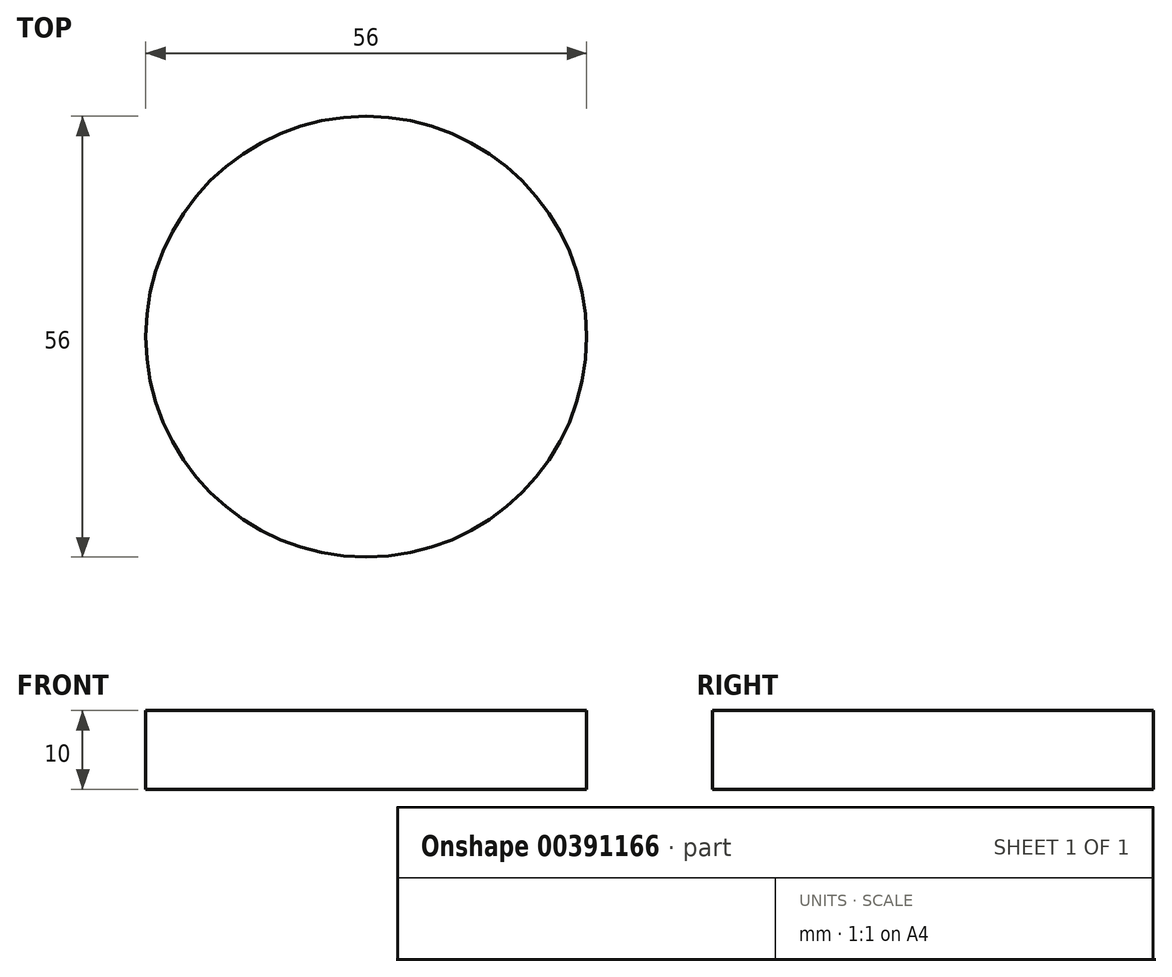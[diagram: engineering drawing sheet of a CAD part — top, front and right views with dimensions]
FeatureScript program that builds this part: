
annotation { "Feature Type Name" : "Feature", "Feature Type Description" : "" }
export const myFeature = defineFeature(function(context is Context, id is Id, definition is map)
    precondition{}
    {
        {
            var Q0;
            Q0=qCreatedBy(makeId("Top.planeOp"),FACE);
            var sketch = newSketch(context, id + "F0", { "sketchPlane" : qUnion([Q0])});
            skCircle(sketch, "E0", {"center": v(0, 0) * mm, "radius": 28 * mm});
            skSolve(sketch);
        }
        {
            var Q0;
            Q0=makeQuery(id+"F0.imprint","IMPRINT",FACE,{"disambiguationData":[TD([[makeQuery(id+"F0.imprint","IMPRINT",EDGE,{"derivedFrom":sQuery(id+"F0.wireOp",EDGE,"E0")}),1.0]])]});
            extrude(context, id + "F1", {"entities" : qUnion([Q0]), "depth" : 10 * mm});
        }
    });
